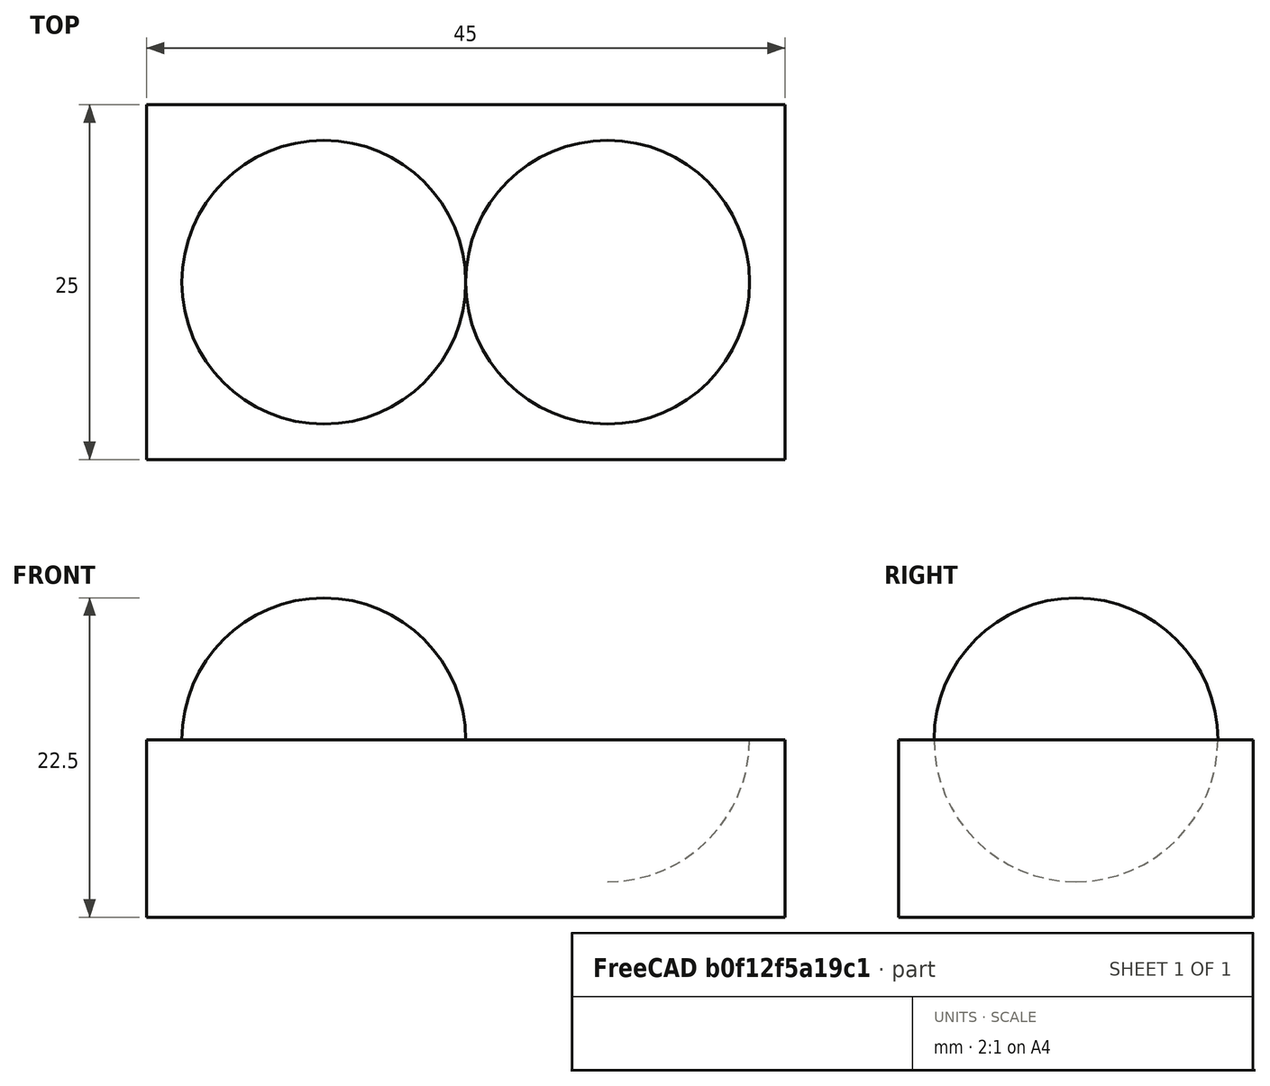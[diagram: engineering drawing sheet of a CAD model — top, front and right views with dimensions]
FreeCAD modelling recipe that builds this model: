
FCSTD DOCUMENT  (FreeCAD 0.18.3R)
Label: finish
License: All rights reserved
LicenseURL: http://en.wikipedia.org/wiki/All_rights_reserved
objects: Part::Sphere×2, Part::Box×1, Part::Fuse×1, Part::Cut×1
note: 5 computed .brp shape members not serialized (recipe doc carries the construction recipe); baked Part::Feature solids carry a one-line shape summary decoded from their .brp

FEATURE [Part::Sphere] Sphere
  Angle1 = -90
  Angle2 = 90
  Angle3 = 360
  AttacherType = Attacher::AttachEngine3D
  Placement = pos=(10,0,0) rot=(0,0,1;0rad)
  Radius = 10
FEATURE [Part::Sphere] Sphere001
  Angle1 = -90
  Angle2 = 90
  Angle3 = 360
  AttacherType = Attacher::AttachEngine3D
  Placement = pos=(30,0,0) rot=(0,0,1;0rad)
  Radius = 10
FEATURE [Part::Box] Box  label="Cube"
  AttacherType = Attacher::AttachEngine3D
  Height = 12.5
  Length = 45
  Placement = pos=(-2.5,-12.5,-12.5) rot=(0,0,1;0rad)
  Width = 25
FEATURE [Part::Fuse] Fusion
  Base = -> Sphere
  Tool = -> Box
FEATURE [Part::Cut] Cut
  Base = -> Fusion
  Tool = -> Sphere001
